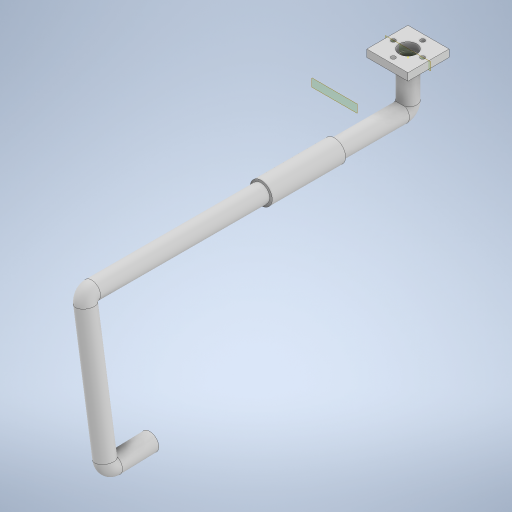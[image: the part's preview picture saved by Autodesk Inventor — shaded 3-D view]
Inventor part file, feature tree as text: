
AUTODESK INVENTOR PART (.ipt)
format: ipt  version: 2023 (Build 270158000, 158)  size: 359,424 bytes
history: native  units: mm
features: sketch x8, extrude x3, plane x2, sweep x1, chamfer x1
ambient origin geometry x8: Origin, YZ Plane, XZ Plane, XY Plane, X Axis, Y Axis, Z Axis, Center Point
bodies: Solid1 (feature_tree)
feature tree (15):
  extrude  "Extrusion1"  Depth=28.0mm
  extrude  "Extrusion2"  Depth=14.0mm
  plane  "Work Plane1"
  sketch  "Sketch3"  dims[d4=5.0mm d5=0.0mm d6=12.0mm]
  sketch  "3D Sketch1"
  sketch  "3D Sketch2"
  sweep  "Sweep1"
  chamfer  "Chamfer1"  Distance=40.0mm Angle=360.0deg
  sketch  "Sketch5"  dims[d8=10.0mm d9=40.0mm d11=360.0deg]
  plane  "Work Plane2"
  extrude  "Extrusion3"  [1 undecoded]
  sketch  "Sketch1"  dims[d0=28.0mm d1=28.0mm]
  sketch  "Sketch2"  dims[d2=14.0mm d3=14.0mm]
  sketch  "Sketch4"  dims[d7=3.0mm]
  sketch  "Sketch6"  dims[d13=5.0mm d14=0.0mm d15=-14.0mm d16=30.0mm d17=220.0mm d18=5.0mm d19=10.0mm d20=0.0mm d21=0.0mm d22=12.0mm d23=1.0mm d24=2.0mm d25=45.0deg d26=95.0mm d27=13.962634mm d28=5.0mm d29=30.0mm d30=90.0deg d31=5.0mm d32=90.0deg d33=-50.0mm d34=15.0mm d35=50.0mm d36=0.0mm]
note: 1 required parameter value undecoded (feature->parameter linkage not recoverable at this tier; creation-order binding heuristic only, values carry confidence <= 0.55)
